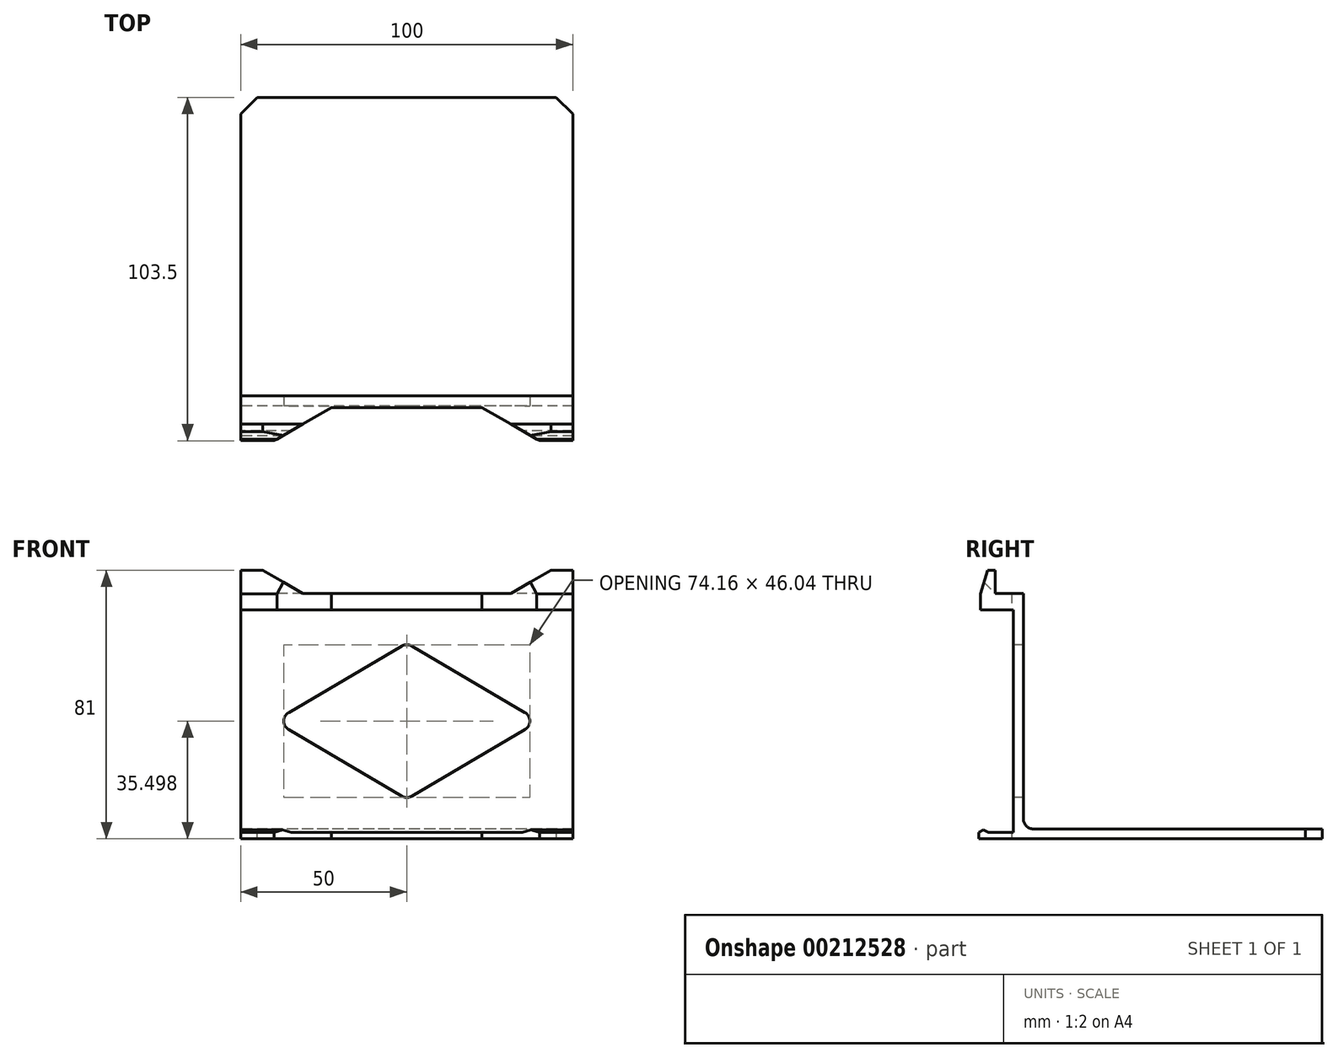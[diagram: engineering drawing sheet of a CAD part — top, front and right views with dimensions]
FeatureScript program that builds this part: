
annotation { "Feature Type Name" : "Feature", "Feature Type Description" : "" }
export const myFeature = defineFeature(function(context is Context, id is Id, definition is map)
    precondition{}
    {
        {
            var Q0;
            Q0=qCreatedBy(makeId("Right.planeOp"),FACE);
            var sketch = newSketch(context, id + "F0", { "sketchPlane" : qUnion([Q0])});
            skLineSegment(sketch, "E0", {"start": v(-3.8, -10.93) * mm, "end": v(-3.8, 56.07) * mm});
            skLineSegment(sketch, "E1", {"start": v(-3.8, 56.07) * mm, "end": v(-13.8, 56.07) * mm});
            skLineSegment(sketch, "E2", {"start": v(-13.8, 56.07) * mm, "end": v(-13.8, 60.9) * mm});
            skLineSegment(sketch, "E3", {"start": v(-11.56, 68.07) * mm, "end": v(-9.3, 68.07) * mm});
            skLineSegment(sketch, "E4", {"start": v(-9.3, 68.07) * mm, "end": v(-9.3, 61.07) * mm});
            skLineSegment(sketch, "E5", {"start": v(-9.3, 61.07) * mm, "end": v(-0.8, 61.07) * mm});
            skLineSegment(sketch, "E6", {"start": v(-0.8, 61.07) * mm, "end": v(-0.8, -9.93) * mm});
            skLineSegment(sketch, "E7", {"start": v(-0.8, -12.93) * mm, "end": v(-14.3, -12.93) * mm});
            skLineSegment(sketch, "E8", {"start": v(-14.3, -12.93) * mm, "end": v(-14.3, -10.93) * mm});
            skLineSegment(sketch, "E9", {"start": v(-11.3, -10.93) * mm, "end": v(-3.8, -10.93) * mm});
            skLineSegment(sketch, "E10", {"start": v(-0.8, -12.93) * mm, "end": v(89.2, -12.93) * mm});
            skLineSegment(sketch, "E11", {"start": v(89.2, -12.93) * mm, "end": v(89.2, -9.93) * mm});
            skLineSegment(sketch, "E12", {"start": v(89.2, -9.93) * mm, "end": v(-0.8, -9.93) * mm});
            skLineSegment(sketch, "E13", {"start": v(-11.56, 68.07) * mm, "end": v(-13.8, 60.9) * mm});
            skPoint(sketch, "E14.orphan", {"position": v(-13.8, 68.07) * mm});
            skLineSegment(sketch, "E15", {"start": v(-11.3, -10.93) * mm, "end": v(-12.8, -10.18) * mm});
            skLineSegment(sketch, "E16", {"start": v(-12.8, -10.18) * mm, "end": v(-14.3, -10.93) * mm});
            skSolve(sketch);
        }
        {
            var Q0;
            Q0=makeQuery(id+"F0.imprint","IMPRINT",FACE,{"disambiguationData":[TD([[makeQuery(id+"F0.imprint","IMPRINT",EDGE,{"derivedFrom":sQuery(id+"F0.wireOp",EDGE,"E0")}),-1.0]])]});
            extrude(context, id + "F1", {"entities" : qUnion([Q0]), "endBound" : BoundingType.SYMMETRIC, "depth" : 100 * mm});
        }
        {
            var Q0;
            Q0=makeQuery(id+"F1.opExtrude","CAP_EDGE",EDGE,{"disambiguationData":[OSD([sQuery(id+"F0.wireOp",EDGE,"E11")])],"isStart":false});
            var Q1;
            Q1=makeQuery(id+"F1.opExtrude","CAP_EDGE",EDGE,{"disambiguationData":[OSD([sQuery(id+"F0.wireOp",EDGE,"E11")])],"isStart":true});
            chamfer(context, id + "F2", {"entities" : qUnion([Q0, Q1]), "width" : 5 * mm, "tangentPropagation" : true});
        }
        {
            var Q0;
            Q0=makeQuery(id+"F1.opExtrude","SWEPT_EDGE",EDGE,{"disambiguationData":[OSD([sQuery(id+"F0.wireOp",EDGE,"E6"),sQuery(id+"F0.wireOp",EDGE,"E12")])]});
            fillet(context, id + "F3", {"entities" : qUnion([Q0]), "radius" : 3 * mm, "tangentPropagation" : true, "allowEdgeOverflow" : false});
        }
        {
            var Q0;
            Q0=makeQuery(id+"F1.opExtrude","SWEPT_FACE",FACE,{"disambiguationData":[OSD([sQuery(id+"F0.wireOp",EDGE,"E7"),sQuery(id+"F0.wireOp",EDGE,"E10")])]});
            var sketch = newSketch(context, id + "F4", { "sketchPlane" : qUnion([Q0])});
            skLineSegment(sketch, "E17", {"start": v(-50, 14.3) * mm, "end": v(-40, 14.3) * mm, "construction": true});
            skLineSegment(sketch, "E18", {"start": v(-40, 14.3) * mm, "end": v(-22.68, 4.3) * mm});
            skLineSegment(sketch, "E19", {"start": v(0, 1.3) * mm, "end": v(0, 4.3) * mm, "construction": true});
            skLineSegment(sketch, "E20", {"start": v(0, 4.3) * mm, "end": v(-22.68, 4.3) * mm});
            skLineSegment(sketch, "E21.MirrorCS", {"start": v(40, 14.3) * mm, "end": v(22.68, 4.3) * mm});
            skLineSegment(sketch, "E22.MirrorCS", {"start": v(0, 4.3) * mm, "end": v(22.68, 4.3) * mm});
            skLineSegment(sketch, "E23", {"start": v(-40, 14.3) * mm, "end": v(40, 14.3) * mm});
            skSolve(sketch);
        }
        {
            var Q0;
            Q0=makeQuery(id+"F4.imprint","IMPRINT",FACE,{"disambiguationData":[TD([[makeQuery(id+"F4.imprint","IMPRINT",EDGE,{"derivedFrom":sQuery(id+"F4.wireOp",EDGE,"E18")}),1.0]])]});
            extrude(context, id + "F5", {"entities" : qUnion([Q0]), "operationType" : NewBodyOperationType.REMOVE, "endBound" : BoundingType.THROUGH_ALL, "oppositeDirection" : true, "depth" : 25 * mm});
        }
        {
            var Q0;
            {var subQ1=sQuery(id+"F0.wireOp",EDGE,"E4");Q0=makeQuery(id+"F5.boolean.opBoolean","SPLIT",FACE,{"disambiguationData":[TD([makeQuery(id+"F5.opExtrude","SWEPT_FACE",FACE,{"disambiguationData":[OSD([sQuery(id+"F4.wireOp",EDGE,"E21.MirrorCS")])]})])],"derivedFrom":makeQuery(id+"F1.opExtrude","SWEPT_FACE",FACE,{"disambiguationData":[OSD([subQ1])]})});}
            var sketch = newSketch(context, id + "F6", { "sketchPlane" : qUnion([Q0])});
            skLineSegment(sketch, "E24", {"start": v(-31.34, 61.07) * mm, "end": v(-43.46, 68.07) * mm});
            skLineSegment(sketch, "E25", {"start": v(-43.46, 68.07) * mm, "end": v(-31.34, 68.07) * mm});
            skLineSegment(sketch, "E26", {"start": v(-31.34, 68.07) * mm, "end": v(-31.34, 61.07) * mm});
            skLineSegment(sketch, "E27.MirrorCS", {"start": v(31.34, 61.07) * mm, "end": v(43.46, 68.07) * mm});
            skLineSegment(sketch, "E28.MirrorCS", {"start": v(43.46, 68.07) * mm, "end": v(31.34, 68.07) * mm});
            skLineSegment(sketch, "E29.MirrorCS", {"start": v(31.34, 68.07) * mm, "end": v(31.34, 61.07) * mm});
            skSolve(sketch);
        }
        {
            var Q0;
            Q0=makeQuery(id+"F6.imprint","IMPRINT",FACE,{"disambiguationData":[TD([[makeQuery(id+"F6.imprint","IMPRINT",EDGE,{"derivedFrom":sQuery(id+"F6.wireOp",EDGE,"E24")}),-1.0]])]});
            var Q1;
            Q1=makeQuery(id+"F6.imprint","IMPRINT",FACE,{"disambiguationData":[TD([[makeQuery(id+"F6.imprint","IMPRINT",EDGE,{"derivedFrom":sQuery(id+"F6.wireOp",EDGE,"E27.MirrorCS")}),1.0]])]});
            extrude(context, id + "F7", {"entities" : qUnion([Q0, Q1]), "operationType" : NewBodyOperationType.REMOVE, "endBound" : BoundingType.UP_TO_NEXT, "oppositeDirection" : true, "depth" : 25 * mm});
        }
        {
            var Q0;
            Q0=makeQuery(id+"F1.opExtrude","SWEPT_FACE",FACE,{"disambiguationData":[OSD([sQuery(id+"F0.wireOp",EDGE,"E0")])]});
            var sketch = newSketch(context, id + "F8", { "sketchPlane" : qUnion([Q0])});
            skLineSegment(sketch, "E30", {"start": v(-50, 22.57) * mm, "end": v(-40, 22.57) * mm, "construction": true});
            skLineSegment(sketch, "E31", {"start": v(0, 56.07) * mm, "end": v(0, 46.07) * mm, "construction": true});
            skPoint(sketch, "E31.endSnap0", {"position": v(0, 56.07) * mm});
            skLineSegment(sketch, "E32", {"start": v(-40, 22.57) * mm, "end": v(0, 46.07) * mm});
            skLineSegment(sketch, "E33.MirrorCS", {"start": v(-40, 22.57) * mm, "end": v(0, -0.93) * mm});
            skLineSegment(sketch, "E34.MirrorCS", {"start": v(40, 22.57) * mm, "end": v(0, 46.07) * mm});
            skLineSegment(sketch, "E35.MirrorCS", {"start": v(40, 22.57) * mm, "end": v(0, -0.93) * mm});
            skSolve(sketch);
        }
        {
            var Q0;
            Q0=makeQuery(id+"F8.imprint","IMPRINT",FACE,{"disambiguationData":[TD([[makeQuery(id+"F8.imprint","IMPRINT",EDGE,{"derivedFrom":sQuery(id+"F8.wireOp",EDGE,"E32")}),-1.0]])]});
            extrude(context, id + "F9", {"entities" : qUnion([Q0]), "operationType" : NewBodyOperationType.REMOVE, "endBound" : BoundingType.UP_TO_NEXT, "oppositeDirection" : true, "depth" : 25 * mm});
        }
        {
            var Q0;
            Q0=makeQuery(id+"F9.boolean.opBoolean","COPY",EDGE,{"derivedFrom":makeQuery(id+"F9.opExtrude","SWEPT_EDGE",EDGE,{"disambiguationData":[OSD([sQuery(id+"F8.wireOp",EDGE,"E32"),sQuery(id+"F8.wireOp",EDGE,"E33.MirrorCS")])]})});
            var Q1;
            Q1=makeQuery(id+"F9.boolean.opBoolean","COPY",EDGE,{"derivedFrom":makeQuery(id+"F9.opExtrude","SWEPT_EDGE",EDGE,{"disambiguationData":[OSD([sQuery(id+"F8.wireOp",EDGE,"E32"),sQuery(id+"F8.wireOp",EDGE,"E34.MirrorCS")])]})});
            var Q2;
            Q2=makeQuery(id+"F9.boolean.opBoolean","COPY",EDGE,{"derivedFrom":makeQuery(id+"F9.opExtrude","SWEPT_EDGE",EDGE,{"disambiguationData":[OSD([sQuery(id+"F8.wireOp",EDGE,"E34.MirrorCS"),sQuery(id+"F8.wireOp",EDGE,"E35.MirrorCS")])]})});
            var Q3;
            Q3=makeQuery(id+"F9.boolean.opBoolean","COPY",EDGE,{"derivedFrom":makeQuery(id+"F9.opExtrude","SWEPT_EDGE",EDGE,{"disambiguationData":[OSD([sQuery(id+"F8.wireOp",EDGE,"E33.MirrorCS"),sQuery(id+"F8.wireOp",EDGE,"E35.MirrorCS")])]})});
            fillet(context, id + "F10", {"entities" : qUnion([Q0, Q1, Q2, Q3]), "radius" : 3 * mm, "tangentPropagation" : true, "allowEdgeOverflow" : false});
        }
    });
